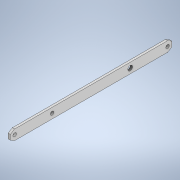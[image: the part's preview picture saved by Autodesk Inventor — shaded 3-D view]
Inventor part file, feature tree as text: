
AUTODESK INVENTOR PART (.ipt)
format: ipt  version: 2020 (Build 240168000, 168)  size: 216,576 bytes
history: native  units: in
note: dims shown in document units (in); Inventor stores cm internally (conversion verified against a paired STEP export)
features: extrude x5, sketch x5, other x3, projected_geometry x3
ambient origin geometry x8: Origin, YZ Plane, XZ Plane, XY Plane, X Axis, Y Axis, Z Axis, Center Point
bodies: Solid1 (feature_tree)
feature tree (16):
  other  "HexWheelGuard.ipt"
  extrude  "Extrusion1"  TaperAngle=0.0deg  [1 undecoded]
  extrude  "Extrusion2"  Depth=0.3937in
  extrude  "Extrusion3"  Depth=0.3937in TaperAngle=0.0deg
  extrude  "Extrusion4"  Depth=0.3543in
  extrude  "Extrusion5"  Depth=0.0787in
  other  "Solid1::HexWheelGuard.ipt"
  other  "TaggingFeature1"
  sketch  "Sketch1"  dims[d0=0.3937in d1=0.0in d2=0.0in]
  projected_geometry  "Projected Loop1"
  sketch  "Sketch2"  dims[d3=0.3937in d4=0.0in d5=0.122in]
  sketch  "Sketch3"  dims[d6=0.122in d7=0.3937in d8=0.0in]
  sketch  "Sketch4"  dims[d10=0.3937in d11=0.0in d12=0.3543in]
  projected_geometry  "Projected Loop2"
  sketch  "Sketch5"  dims[d13=0.0787in d14=0.0in d15=0.122in d17=1.5748in d18=0.5906in]
  projected_geometry  "Projected Loop3"
note: 1 required parameter value undecoded (feature->parameter linkage not recoverable at this tier; creation-order binding heuristic only, values carry confidence <= 0.55)
